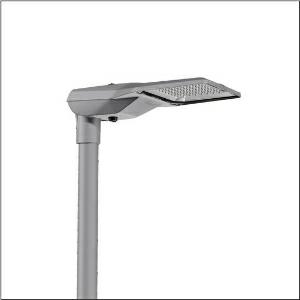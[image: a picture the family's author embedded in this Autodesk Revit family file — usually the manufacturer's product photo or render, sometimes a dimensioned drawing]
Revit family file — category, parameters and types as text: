
# Revit family: streetlight_sl_21_iq_midi___p0_8a_5xe3u31y08mb_3be5
name_source: partatom
category: Lighting Fixtures
units: mm (PartAtom-declared; Revit-internal decimal feet)

## family parameters
Cut with Voids When Loaded = No
Host = Face
Light Source = No
Part Type = Normal
Room Calculation Point = No
Round Connector Dimension = Use Diameter
Shared = No

## types (1)
- --- (1 x LED, 18500 lm, 129.3 W, 3000K)
    Apparent Load = 129 VA
    CIE Flux Codes = 33 69 96 100 100
    Color Rendering = 70
    Color Temperature = 3000K
    Default Elevation = 1800 mm
    Description = Streetlight SL 21 iQ midi, mast luminaire, primary light control with lens, of PMMA, primary optical cover: cover, of toughened safety glass, transparent, light distribution: P0.8a, light emission: direct distribution, primary light characteristic: asymmetric, installation type: post-top, side-entry, LED, High Power LED, rated luminous flux: 18.500lm, luminous efficacy: 143lm/W, light colour: 730, colour temperature: 3000K, control gear: iQ-Street Remote, D4i with power reduction, control: pre-setting: logarithmic dimming characteristic, Street-Remote, Auto-Match, Temp-Guard, Lumen-Switch, Night-Set, Smart-Wire, Light-Fading, Desk-Remote (wireless, voltage-free reading and setting of iQ features in the workshop via application-optimized NFC function/RFID function), optimised constant luminous flux control (CLO 2.0), mains connection: 230..240V, AC, 50/60Hz, start of lifetime: 129W, end of service life: 142W, reduction: 56W, luminaire housing, of diecast aluminium, powder-coated, Siteco® metallic grey (DB 702S), corrosivity category C5 mid according to DIN EN ISO 12944, please order mast flange separately, inclination adjustable: 0°, 5°, 10°, 15°, sealing non-destructively replaceable, multi-level sealing system, length: 644mm, width: 335mm, height: 110mm, mast flange for spigot size: 42mm (side-entry): 5XC10008XM4, 60/48mm (side-entry/post-top): 5XC10108XM2, 76/60mm (side-entry/post-top): 5XC10108XM1, mounting height: 4..8m, Smart Interface below and above, protection rating (complete): IP66, insulation class (complete): insulation class II (safety insulation), certification: CE, ENEC, ENEC+, VDE, impact resistance: IK10, permissible operating ambient temperature for outdoor applications: -40..+50°C, standard-compliant lighting for roads and squares, packaging unit: 1 piece

Light Distribution: P0.8a
    Height = 111 mm
    Lamp = 1 x LED
    Lamp Light Flux = 18500 lm
    Lamp Power = 129.3 W
    Lamp count = 1
    Length = 644 mm
    Luminous efficacy = 143 lm/W
    Manufacturer = Siteco
    ModVariant = No
    Model = 5XE3U31Y08MB
    Number of Poles = 1
    OnlyDefault = Yes
    Power Factor = 1
    Product Name = Streetlight SL 21 iQ midi | P0.8a
    Product group = mast luminaire | pylon top
    ProductGroupID = 6100
    Protection Class = Protection class II
    Protection Degree = IP 66
    RLX_Detail_Level = 1
    RLX_Emergency_Light_Flux = 0 lm
    RLX_Emergency_Type = 0
    RLX_Emergency_Type_DB = No
    RlxData = <blob elided: 90853 chars, md5=1ceec036>
    Socket = socket
    Standby Power = 0 W
    System Light Flux = 18500 lm
    System Power = 129 W
    Type Comments = factory setting: luminous flux: 100 % | dim-lin: 254 | 672 mA
    Type Image = l_1004304.jpg
    URL = http://relux.com
    VarID = @adj_095431
    Voltage = 0 V
    Weight = 0.00 kg
    Width = 336 mm

## geometry (parser evidence)
native form markers: Blend x4, Sweep x11
no freeform markers — native parametric forms only
